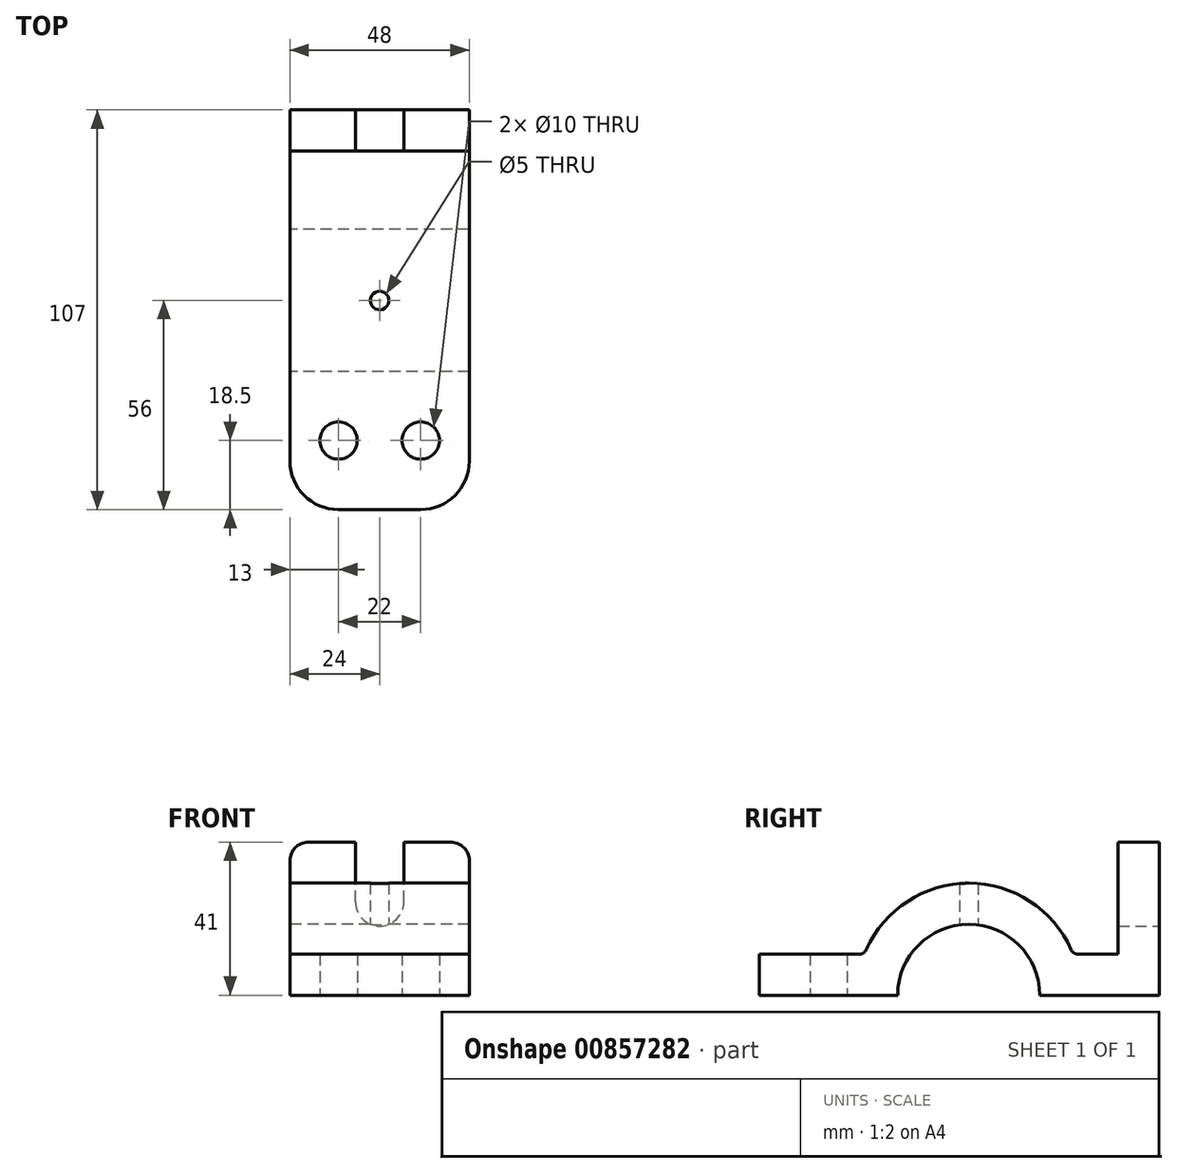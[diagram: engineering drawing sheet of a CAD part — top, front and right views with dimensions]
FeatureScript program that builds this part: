
annotation { "Feature Type Name" : "Feature", "Feature Type Description" : "" }
export const myFeature = defineFeature(function(context is Context, id is Id, definition is map)
    precondition{}
    {
        {
            var Q0;
            Q0=qCreatedBy(makeId("Right.planeOp"),FACE);
            var sketch = newSketch(context, id + "F0", { "sketchPlane" : qUnion([Q0])});
            skCircle(sketch, "E0", {"center": v(0, 0) * mm, "radius": 19 * mm});
            skCircle(sketch, "E1", {"center": v(0, 0) * mm, "radius": 30 * mm});
            skLineSegment(sketch, "E2.bottom", {"start": v(-56, 0) * mm, "end": v(51, 0) * mm});
            skLineSegment(sketch, "E2.top", {"start": v(-56, 11) * mm, "end": v(51, 11) * mm});
            skLineSegment(sketch, "E2.left", {"start": v(-56, 0) * mm, "end": v(-56, 11) * mm});
            skLineSegment(sketch, "E2.right", {"start": v(51, 0) * mm, "end": v(51, 11) * mm});
            skLineSegment(sketch, "E3.bottom", {"start": v(51, 11) * mm, "end": v(40, 11) * mm});
            skLineSegment(sketch, "E3.top", {"start": v(51, 41) * mm, "end": v(40, 41) * mm});
            skLineSegment(sketch, "E3.left", {"start": v(51, 11) * mm, "end": v(51, 41) * mm});
            skLineSegment(sketch, "E3.right", {"start": v(40, 11) * mm, "end": v(40, 41) * mm});
            skSolve(sketch);
        }
        {
            var Q0;
            {var subQ5=sQuery(id+"F0.wireOp",EDGE,"E2.left");Q0=makeQuery(id+"F0.imprint","IMPRINT",FACE,{"disambiguationData":[TD([[makeQuery(id+"F0.imprint","IMPRINT",EDGE,{"derivedFrom":subQ5}),-1.0]])]});}
            var Q1;
            {var subQ0=sQuery(id+"F0.wireOp",EDGE,"E2.bottom");var subQ1=sQuery(id+"F0.wireOp",EDGE,"E0");var subQ2=makeQuery(id+"F0.imprint","INTERSECT",VERTEX,{"disambiguationData":[OD(0.0)],"derivedFrom":[subQ1,subQ0]});Q1=makeQuery(id+"F0.imprint","IMPRINT",FACE,{"disambiguationData":[TD([[makeQuery(id+"F0.imprint","IMPRINT",EDGE,{"disambiguationData":[TD([[subQ2,1.0]])],"derivedFrom":subQ1}),-1.0]])]});}
            var Q2;
            {var subQ0=sQuery(id+"F0.wireOp",EDGE,"E2.top");var subQ1=sQuery(id+"F0.wireOp",EDGE,"E0");var subQ2=makeQuery(id+"F0.imprint","INTERSECT",VERTEX,{"disambiguationData":[OD(0.0)],"derivedFrom":[subQ1,subQ0]});Q2=makeQuery(id+"F0.imprint","IMPRINT",FACE,{"disambiguationData":[TD([[makeQuery(id+"F0.imprint","IMPRINT",EDGE,{"disambiguationData":[TD([[subQ2,1.0]])],"derivedFrom":subQ1}),-1.0]])]});}
            var Q3;
            {var subQ0=sQuery(id+"F0.wireOp",EDGE,"E2.top");var subQ1=sQuery(id+"F0.wireOp",EDGE,"E0");var subQ2=makeQuery(id+"F0.imprint","INTERSECT",VERTEX,{"disambiguationData":[OD(1.0)],"derivedFrom":[subQ1,subQ0]});Q3=makeQuery(id+"F0.imprint","IMPRINT",FACE,{"disambiguationData":[TD([[makeQuery(id+"F0.imprint","IMPRINT",EDGE,{"disambiguationData":[TD([[subQ2,1.0]])],"derivedFrom":subQ1}),-1.0]])]});}
            var Q4;
            {var subQ0=sQuery(id+"F0.wireOp",EDGE,"E2.right");Q4=makeQuery(id+"F0.imprint","IMPRINT",FACE,{"disambiguationData":[TD([[makeQuery(id+"F0.imprint","IMPRINT",EDGE,{"derivedFrom":subQ0}),1.0]])]});}
            var Q5;
            Q5=makeQuery(id+"F0.imprint","IMPRINT",FACE,{"disambiguationData":[TD([[makeQuery(id+"F0.imprint","IMPRINT",EDGE,{"derivedFrom":sQuery(id+"F0.wireOp",EDGE,"E3.top")}),1.0]])]});
            extrude(context, id + "F1", {"entities" : qUnion([Q0, Q1, Q2, Q3, Q4, Q5]), "endBound" : BoundingType.SYMMETRIC, "depth" : 48 * mm, "offsetDistance" : 25.4 * mm});
        }
        {
            var Q0;
            Q0=makeQuery(id+"F1.opExtrude","SWEPT_FACE",FACE,{"disambiguationData":[OSD([sQuery(id+"F0.wireOp",EDGE,"E2.right"),sQuery(id+"F0.wireOp",EDGE,"E3.left")])]});
            var sketch = newSketch(context, id + "F2", { "sketchPlane" : qUnion([Q0])});
            skLineSegment(sketch, "E4", {"start": v(0, 0) * mm, "end": v(0, 41) * mm, "construction": true});
            skCircle(sketch, "E5", {"center": v(0, 25) * mm, "radius": 6.5 * mm});
            skLineSegment(sketch, "E6", {"start": v(-6.5, 25) * mm, "end": v(-6.5, 41) * mm});
            skLineSegment(sketch, "E7", {"start": v(6.5, 25) * mm, "end": v(6.5, 41) * mm});
            skSolve(sketch);
        }
        {
            var Q0;
            {var subQ0=sQuery(id+"F2.wireOp",EDGE,"E6");Q0=makeQuery(id+"F2.imprint","IMPRINT",FACE,{"disambiguationData":[TD([[makeQuery(id+"F2.imprint","IMPRINT",EDGE,{"derivedFrom":subQ0}),-1.0]])]});}
            var Q1;
            {var subQ0=sQuery(id+"F2.wireOp",EDGE,"E5");var subQ1=makeQuery(id+"F2.imprint","INTERSECT",VERTEX,{"derivedFrom":[subQ0,sQuery(id+"F2.wireOp",EDGE,"E6")]});Q1=makeQuery(id+"F2.imprint","IMPRINT",FACE,{"disambiguationData":[TD([[makeQuery(id+"F2.imprint","IMPRINT",EDGE,{"disambiguationData":[TD([[subQ1,1.0]])],"derivedFrom":subQ0}),1.0]])]});}
            var Q2;
            Q2=makeQuery(id+"F1.opExtrude","SWEPT_FACE",FACE,{"disambiguationData":[OSD([sQuery(id+"F0.wireOp",EDGE,"E3.right")])]});
            extrude(context, id + "F3", {"entities" : qUnion([Q0, Q1]), "operationType" : NewBodyOperationType.REMOVE, "endBound" : BoundingType.UP_TO_SURFACE, "oppositeDirection" : true, "depth" : 25.4 * mm, "endBoundEntityFace" : qUnion([Q2]), "offsetDistance" : 25.4 * mm});
        }
        {
            var Q0;
            {var subQ0=sQuery(id+"F0.wireOp",EDGE,"E2.bottom");Q0=makeQuery(id+"F1.opExtrude","SWEPT_FACE",FACE,{"disambiguationData":[OSD([subQ0]),TDD([makeQuery(id+"F0.imprint","IMPRINT",EDGE,{"disambiguationData":[TD([[makeQuery(id+"F0.imprint","INTERSECT",VERTEX,{"derivedFrom":[subQ0,sQuery(id+"F0.wireOp",EDGE,"E2.left")]}),-1.0]])],"derivedFrom":subQ0}),makeQuery(id+"F0.imprint","IMPRINT",EDGE,{"disambiguationData":[TD([[makeQuery(id+"F0.imprint","INTERSECT",VERTEX,{"disambiguationData":[OD(0.0)],"derivedFrom":[sQuery(id+"F0.wireOp",EDGE,"E0"),subQ0]}),1.0]])],"derivedFrom":subQ0})])]});}
            var sketch = newSketch(context, id + "F4", { "sketchPlane" : qUnion([Q0])});
            skCircle(sketch, "E8", {"center": v(0, 0) * mm, "radius": 2.5 * mm});
            skLineSegment(sketch, "E9", {"start": v(0, 56) * mm, "end": v(0, 19) * mm, "construction": true});
            skLineSegment(sketch, "E10", {"start": v(24, 37.5) * mm, "end": v(-24, 37.5) * mm, "construction": true});
            skCircle(sketch, "E11", {"center": v(11, 37.5) * mm, "radius": 5 * mm});
            skCircle(sketch, "E12", {"center": v(-11, 37.5) * mm, "radius": 5 * mm});
            skSolve(sketch);
        }
        {
            var Q0;
            Q0=makeQuery(id+"F4.imprint","IMPRINT",FACE,{"disambiguationData":[TD([[makeQuery(id+"F4.imprint","IMPRINT",EDGE,{"derivedFrom":sQuery(id+"F4.wireOp",EDGE,"E11")}),1.0]])]});
            var Q1;
            Q1=makeQuery(id+"F4.imprint","IMPRINT",FACE,{"disambiguationData":[TD([[makeQuery(id+"F4.imprint","IMPRINT",EDGE,{"derivedFrom":sQuery(id+"F4.wireOp",EDGE,"E8")}),1.0]])]});
            var Q2;
            Q2=makeQuery(id+"F4.imprint","IMPRINT",FACE,{"disambiguationData":[TD([[makeQuery(id+"F4.imprint","IMPRINT",EDGE,{"derivedFrom":sQuery(id+"F4.wireOp",EDGE,"E12")}),1.0]])]});
            extrude(context, id + "F5", {"entities" : qUnion([Q0, Q1, Q2]), "operationType" : NewBodyOperationType.REMOVE, "endBound" : BoundingType.THROUGH_ALL, "oppositeDirection" : true, "depth" : 25.4 * mm, "offsetDistance" : 25.4 * mm});
        }
        {
            var Q0;
            Q0=makeQuery(id+"F1.opExtrude","CAP_EDGE",EDGE,{"disambiguationData":[OSD([sQuery(id+"F0.wireOp",EDGE,"E2.left")])],"isStart":true});
            var Q1;
            Q1=makeQuery(id+"F1.opExtrude","CAP_EDGE",EDGE,{"disambiguationData":[OSD([sQuery(id+"F0.wireOp",EDGE,"E2.left")])],"isStart":false});
            fillet(context, id + "F6", {"entities" : qUnion([Q0, Q1]), "radius" : 13 * mm, "tangentPropagation" : true, "allowEdgeOverflow" : false});
        }
        {
            var Q0;
            Q0=makeQuery(id+"F1.opExtrude","CAP_EDGE",EDGE,{"disambiguationData":[OSD([sQuery(id+"F0.wireOp",EDGE,"E3.top")])],"isStart":true});
            var Q1;
            Q1=makeQuery(id+"F1.opExtrude","CAP_EDGE",EDGE,{"disambiguationData":[OSD([sQuery(id+"F0.wireOp",EDGE,"E3.top")])],"isStart":false});
            fillet(context, id + "F7", {"entities" : qUnion([Q0, Q1]), "radius" : 5 * mm, "tangentPropagation" : true, "allowEdgeOverflow" : false});
        }
        {
            var Q0;
            {var subQ0=sQuery(id+"F0.wireOp",EDGE,"E2.top");var subQ1=sQuery(id+"F0.wireOp",EDGE,"E1");Q0=makeQuery(id+"F1.opExtrude","SWEPT_EDGE",EDGE,{"disambiguationData":[OSD([subQ1,subQ0]),TDD([makeQuery(id+"F0.imprint","INTERSECT",VERTEX,{"disambiguationData":[OD(1.0)],"derivedFrom":[subQ1,subQ0]})])]});}
            var Q1;
            {var subQ0=sQuery(id+"F0.wireOp",EDGE,"E2.top");var subQ1=sQuery(id+"F0.wireOp",EDGE,"E1");Q1=makeQuery(id+"F1.opExtrude","SWEPT_EDGE",EDGE,{"disambiguationData":[OSD([subQ1,subQ0]),TDD([makeQuery(id+"F0.imprint","INTERSECT",VERTEX,{"disambiguationData":[OD(0.0)],"derivedFrom":[subQ1,subQ0]})])]});}
            fillet(context, id + "F8", {"entities" : qUnion([Q0, Q1]), "radius" : 2 * mm, "tangentPropagation" : true, "allowEdgeOverflow" : false});
        }
    });
